MODEL slx_987f32f71710
KIND model
BLOCK [Outport] ActualStateEstimateOut
  BusOutputAsStruct = on
  IconDisplay = Port number
  OutDataTypeStr = Bus: VehicleDynamicState
  Port = 2
BLOCK [Inport] ActuatorLimitations
  BusOutputAsStruct = on
  IconDisplay = Port number
  OutDataTypeStr = Bus: ActuatorLimitations
  Port = 5
BLOCK [BusCreator] Bus Creator
  DisplayOption = bar
  InheritFromInputs = on
  Inputs = 14
  Ports = [14, 1]
BLOCK [BusSelector] Bus Selector
  OutputAsBus = off
  OutputSignals = dot_d_numerical_mps,x_pred_m,y_pred_m,x_pred_left_m,y_pred_left_m,x_pred_right_m,y_pred_right_m,vx_pred_mps
  Ports = [1, 8]
BLOCK [BusSelector] Bus Selector1
  OutputAsBus = off
  OutputSignals = mvdc_path_matching_debug.PathPos.d_m,mvdc_path_matching_debug.ActualTrajPoint.tube_l_m,mvdc_path_matching_debug.ActualTrajPoint.tube_r_m
  Ports = [1, 3]
BLOCK [BusSelector] Bus Selector2
  OutputAsBus = off
  OutputSignals = mvdc_tmpc_fast_debug.LatAcc_FB_Dist_rad,mvdc_tmpc_fast_debug.LatAcc_FB_ay_rad,mvdc_tmpc_fast_debug.LatAcc_FFss_rad
  Ports = [1, 3]
BLOCK [Outport] ControllerLearning_Send
  BusOutputAsStruct = on
  IconDisplay = Port number
  OutDataTypeStr = Bus: ControllerLearning_Send
  Port = 6
BLOCK [Outport] Debug
  BusOutputAsStruct = on
  IconDisplay = Port number
  OutDataTypeStr = Bus: mvdc_vehicle_dynamics_control_debug
BLOCK [ModelReference] DebugParsing
  ModelNameDialog = mloc_debug_mes.slx
  ModelReferenceVersion = 1.105
  Ports = [6, 1]
BLOCK [Inport] ExternalDebug
  IconDisplay = Port number
  OutDataTypeStr = Bus: ExternalDebug
  Port = 2
BLOCK [From] From1
  GotoTag = TUMModeControl
BLOCK [From] From2
  GotoTag = mvdc_tube_mpc_debug
BLOCK [From] From25
  GotoTag = ActualEstimateBasedState
BLOCK [From] From29
  GotoTag = TUMModeControl
BLOCK [From] From3
  GotoTag = mvdc_trajectory_driver_debug_all
BLOCK [From] From31
  GotoTag = mloc_statemachine_debug
BLOCK [From] From34
  GotoTag = mvdc_state_estimation_debug
BLOCK [From] From4
  GotoTag = StatusDriver
BLOCK [Goto] Goto1
  GotoTag = mvdc_tube_mpc_debug
BLOCK [Goto] Goto14
  GotoTag = mvdc_trajectory_driver_debug_all
BLOCK [Goto] Goto16
  GotoTag = TUMModeControl
BLOCK [Goto] Goto27
  GotoTag = mloc_statemachine_debug
BLOCK [Goto] Goto30
  GotoTag = mvdc_state_estimation_debug
BLOCK [Goto] Goto6
  GotoTag = StatusDriver
BLOCK [Goto] Goto7
  GotoTag = ActualEstimateBasedState
BLOCK [Outport] LiveVisualization_Send
  BusOutputAsStruct = on
  IconDisplay = Port number
  OutDataTypeStr = Bus: LiveVisualization
  Port = 8
  PortDimensions = 1
BLOCK [Memory] Memory
BLOCK [Memory] Memory1
  InitialCondition = IC_TUMModeControl
BLOCK [SignalConversion] Signal Copy
  OverrideOpt = off
BLOCK [SignalConversion] Signal Copy1
  OverrideOpt = off
BLOCK [SignalConversion] Signal Copy2
  OverrideOpt = off
BLOCK [SignalConversion] Signal Copy3
  OverrideOpt = off
BLOCK [ModelReference] StateEstimation
  ModelNameDialog = mvdc_state_estimation
  ModelReferenceVersion = 1.978
  Ports = [3, 3]
BLOCK [ModelReference] Statemachine
  ModelNameDialog = mloc_statemachine.slx
  ModelReferenceVersion = 1.485
  Ports = [3, 2]
BLOCK [Outport] TUMModeControl
  BusOutputAsStruct = on
  IconDisplay = Port number
  OutDataTypeStr = Bus: TUMModeControl
  Port = 3
  PortDimensions = 1
BLOCK [Inport] TrajectoryPlanning
  BusOutputAsStruct = on
  IconDisplay = Port number
  OutDataTypeStr = Bus: TrajectoryPlanning
BLOCK [ModelReference] TrajectoryTracking
  ModelNameDialog = mvdc_trajectory_driver.slx
  ModelReferenceVersion = 1.1202
  Ports = [6, 6]
BLOCK [Outport] VehicleControl
  BusOutputAsStruct = on
  IconDisplay = Port number
  OutDataTypeStr = Bus: VehicleControl
  Port = 5
BLOCK [Inport] VehicleSensorData
  BusOutputAsStruct = on
  IconDisplay = Port number
  OutDataTypeStr = Bus: VehicleSensorData
  Port = 3
BLOCK [Inport] VehicleSystemStatus
  BusOutputAsStruct = on
  IconDisplay = Port number
  OutDataTypeStr = Bus: VehicleSystemStatus
  Port = 4
BLOCK [Outport] VisualLoc_Send
  BusOutputAsStruct = on
  IconDisplay = Port number
  OutDataTypeStr = Bus: VisualLoc_Send
  Port = 4
BLOCK [Outport] mvdc_tube_mpc_debug
  IconDisplay = Port number
  OutDataTypeStr = Bus: mvdc_tube_mpc_debug
  Port = 7
  SampleTime = tS
ANNOTATION (root): Author: Alexander Wischnewski (<email>) Chair of Automatic Control at TU Munich Description: Implements the full software necessary to drive an autonomous race car. It is designed to be vehicle independent and can be reconfigured for use with different vehicles by parameter changes only, as long as the outside interfaces are kept. The Statemachine handles the vehicle startup and safety checks. The...<+1278ch>
ANNOTATION (root): Communication Status and Diagnosis
ANNOTATION (root): State machine
ANNOTATION (root): Vehicle Dynamics Control
LINE ActuatorLimitations:1 -> TrajectoryTracking:5
LINE Bus Creator:1 -> LiveVisualization_Send:1
LINE Bus Selector1:1 -> Signal Copy:1
LINE Bus Selector1:2 -> Signal Copy1:1
LINE Bus Selector1:3 -> Signal Copy2:1
LINE Bus Selector2:1 -> Bus Creator:12
LINE Bus Selector2:2 -> Bus Creator:13
LINE Bus Selector2:3 -> Bus Creator:14
LINE Bus Selector:1 -> Signal Copy3:1
LINE Bus Selector:2 -> Bus Creator:5
LINE Bus Selector:3 -> Bus Creator:6
LINE Bus Selector:4 -> Bus Creator:7
LINE Bus Selector:5 -> Bus Creator:8
LINE Bus Selector:6 -> Bus Creator:9
LINE Bus Selector:7 -> Bus Creator:10
LINE Bus Selector:8 -> Bus Creator:11
LINE DebugParsing:1 -> Debug:1
LINE ExternalDebug:1 -> DebugParsing:5
LINE From1:1 -> TrajectoryTracking:2
LINE From25:1 -> Statemachine:2
LINE From29:1 -> StateEstimation:1
LINE From2:1 -> DebugParsing:4
LINE From31:1 -> DebugParsing:3
LINE From34:1 -> DebugParsing:2
LINE From3:1 -> DebugParsing:1
LINE From4:1 -> Statemachine:3
LINE Memory1:1 -> Goto16:1
LINE Memory:1 -> StateEstimation:3
LINE Signal Copy1:1 -> Bus Creator:3
LINE Signal Copy2:1 -> Bus Creator:4
LINE Signal Copy3:1 -> Bus Creator:2
LINE Signal Copy:1 -> Bus Creator:1
NET StateEstimation:1 -> ActualStateEstimateOut:1, Goto7:1, TrajectoryTracking:3
LINE StateEstimation:2 -> Goto30:1
LINE StateEstimation:3 -> VisualLoc_Send:1
LINE Statemachine:1 -> Goto27:1
NET Statemachine:2 -> Memory1:1, TUMModeControl:1
LINE TrajectoryPlanning:1 -> TrajectoryTracking:4
LINE TrajectoryTracking:1 -> Goto6:1
NET TrajectoryTracking:2 -> Bus Selector1:1, Bus Selector2:1, Goto14:1
LINE TrajectoryTracking:3 -> ControllerLearning_Send:1
LINE TrajectoryTracking:4 -> VehicleControl:1
NET TrajectoryTracking:5 -> Bus Selector:1, Goto1:1, mvdc_tube_mpc_debug:1
LINE TrajectoryTracking:6 -> Memory:1
NET VehicleSensorData:1 -> DebugParsing:6, StateEstimation:2, TrajectoryTracking:6
NET VehicleSystemStatus:1 -> Statemachine:1, TrajectoryTracking:1
note: NET lines group one-source signal fan-out (src -> all destinations, sorted); 1:1 wires keep LINE
